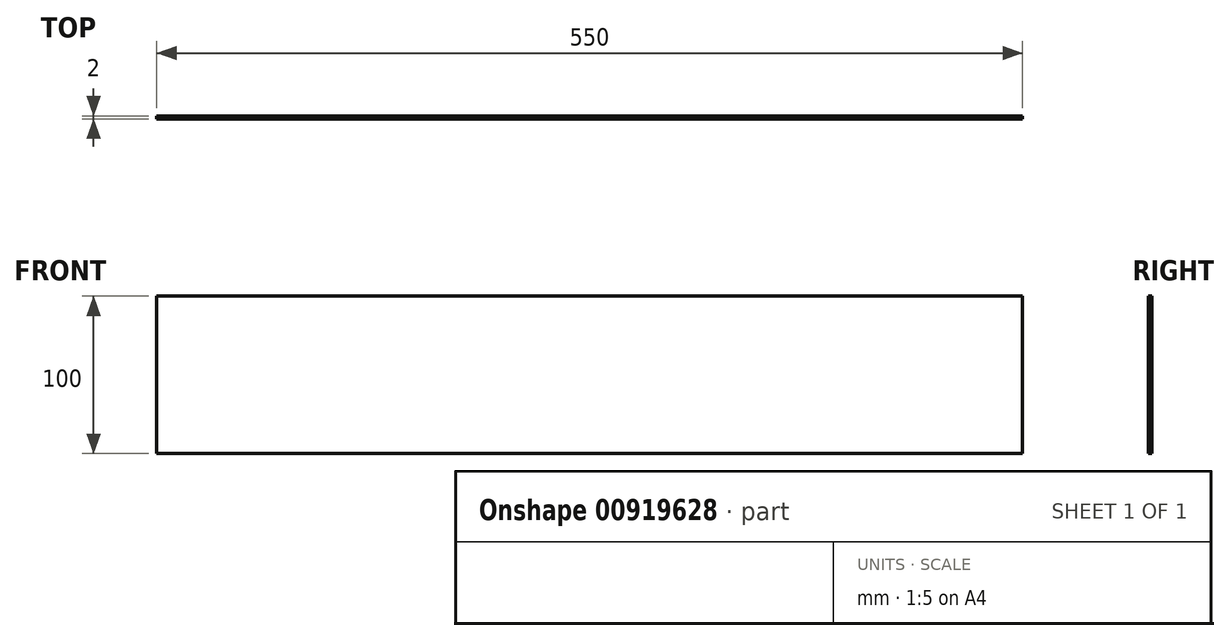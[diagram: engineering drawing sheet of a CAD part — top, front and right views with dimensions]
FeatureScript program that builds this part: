
annotation { "Feature Type Name" : "Feature", "Feature Type Description" : "" }
export const myFeature = defineFeature(function(context is Context, id is Id, definition is map)
    precondition{}
    {
        {
            var Q0;
            Q0=qCreatedBy(makeId("Front.planeOp"),FACE);
            var sketch = newSketch(context, id + "F0", { "sketchPlane" : qUnion([Q0])});
            skLineSegment(sketch, "E0.rect.bottom", {"start": v(275, -50) * mm, "end": v(-275, -50) * mm});
            skLineSegment(sketch, "E0.rect.top", {"start": v(275, 50) * mm, "end": v(-275, 50) * mm});
            skLineSegment(sketch, "E0.rect.left", {"start": v(275, -50) * mm, "end": v(275, 50) * mm});
            skLineSegment(sketch, "E0.rect.right", {"start": v(-275, -50) * mm, "end": v(-275, 50) * mm});
            skPoint(sketch, "E0.rect.middle", {"position": v(0, 0) * mm});
            skSolve(sketch);
        }
        {
            var Q0;
            Q0=qSketchRegion(id+"F0",true);
            extrude(context, id + "F1", {"entities" : qUnion([Q0]), "depth" : 2 * mm});
        }
    });
